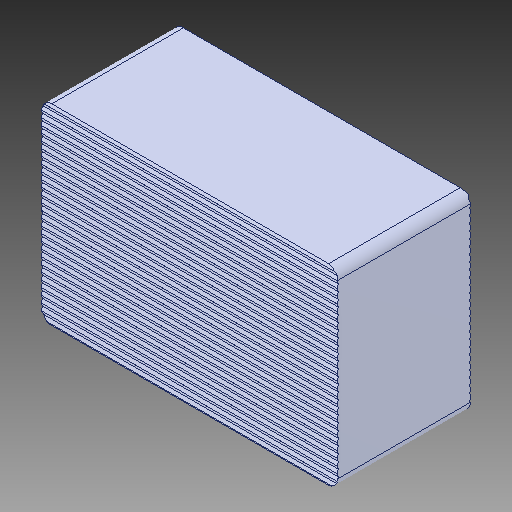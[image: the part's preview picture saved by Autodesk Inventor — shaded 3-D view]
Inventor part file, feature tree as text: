
AUTODESK INVENTOR PART (.ipt)
format: ipt  version: 2018 (Build 220112000, 112)  size: 241,152 bytes
history: native  units: in
note: dims shown in document units (in); Inventor stores cm internally (conversion verified against a paired STEP export)
features: mirror x1
ambient origin geometry x8: Origin, YZ Plane, XZ Plane, XY Plane, X Axis, Y Axis, Z Axis, Center Point
bodies: Solid1 (feature_tree)
feature tree (1):
  mirror  "Mirror1"
